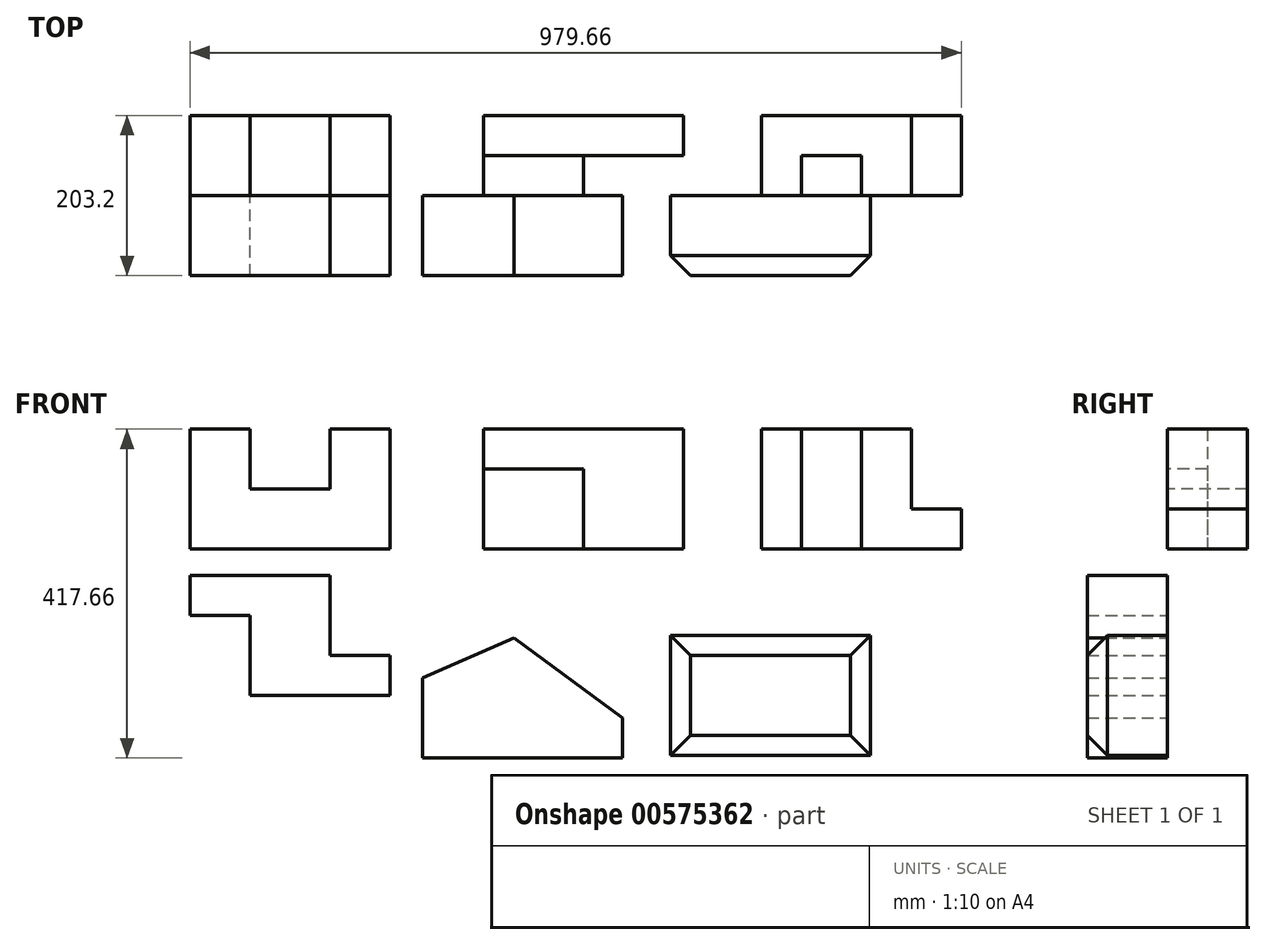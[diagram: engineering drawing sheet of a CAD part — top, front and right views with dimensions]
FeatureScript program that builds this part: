
annotation { "Feature Type Name" : "Feature", "Feature Type Description" : "" }
export const myFeature = defineFeature(function(context is Context, id is Id, definition is map)
    precondition{}
    {
        {
            var Q0;
            Q0=qCreatedBy(makeId("Front.planeOp"),FACE);
            var sketch = newSketch(context, id + "F0", { "sketchPlane" : qUnion([Q0])});
            skLineSegment(sketch, "E0", {"start": v(0, 0) * mm, "end": v(254, 0) * mm});
            skLineSegment(sketch, "E1", {"start": v(254, 0) * mm, "end": v(254, 152.4) * mm});
            skLineSegment(sketch, "E2", {"start": v(254, 152.4) * mm, "end": v(177.8, 152.4) * mm});
            skLineSegment(sketch, "E3", {"start": v(177.8, 152.4) * mm, "end": v(177.8, 76.2) * mm});
            skLineSegment(sketch, "E4", {"start": v(177.8, 76.2) * mm, "end": v(76.2, 76.2) * mm});
            skLineSegment(sketch, "E5", {"start": v(76.2, 76.2) * mm, "end": v(76.2, 152.4) * mm});
            skLineSegment(sketch, "E6", {"start": v(76.2, 152.4) * mm, "end": v(0, 152.4) * mm});
            skLineSegment(sketch, "E7", {"start": v(0, 152.4) * mm, "end": v(0, 0) * mm});
            skSolve(sketch);
        }
        {
            var Q0;
            Q0=makeQuery(id+"F0.imprint","IMPRINT",FACE,{"disambiguationData":[TD([[makeQuery(id+"F0.imprint","IMPRINT",EDGE,{"derivedFrom":sQuery(id+"F0.wireOp",EDGE,"E0")}),1.0]])]});
            extrude(context, id + "F1", {"entities" : qUnion([Q0]), "oppositeDirection" : true, "depth" : 101.6 * mm, "offsetDistance" : 25.4 * mm});
        }
        {
            var Q0;
            Q0=qCreatedBy(makeId("Top.planeOp"),FACE);
            var sketch = newSketch(context, id + "F2", { "sketchPlane" : qUnion([Q0])});
            skLineSegment(sketch, "E8", {"start": v(372.49, 0) * mm, "end": v(372.49, 101.6) * mm});
            skLineSegment(sketch, "E9", {"start": v(372.49, 101.6) * mm, "end": v(626.49, 101.6) * mm});
            skLineSegment(sketch, "E10", {"start": v(626.49, 101.6) * mm, "end": v(626.49, 50.8) * mm});
            skLineSegment(sketch, "E11", {"start": v(626.49, 50.8) * mm, "end": v(499.49, 50.8) * mm});
            skLineSegment(sketch, "E12", {"start": v(499.49, 50.8) * mm, "end": v(499.49, 0) * mm});
            skLineSegment(sketch, "E13", {"start": v(499.49, 0) * mm, "end": v(372.49, 0) * mm});
            skSolve(sketch);
        }
        {
            var Q0;
            Q0 = qSketchRegion(id + "F2", true);
            extrude(context, id + "F3", {"entities" : qUnion([Q0]), "depth" : 152.4 * mm, "offsetDistance" : 25.4 * mm});
        }
        {
            var Q0;
            Q0=makeQuery(id+"F3.opExtrude","SWEPT_FACE",FACE,{"disambiguationData":[OSD([sQuery(id+"F2.wireOp",EDGE,"E13")])]});
            var sketch = newSketch(context, id + "F4", { "sketchPlane" : qUnion([Q0])});
            skLineSegment(sketch, "E14.bottom", {"start": v(372.49, 152.4) * mm, "end": v(499.49, 152.4) * mm});
            skLineSegment(sketch, "E14.top", {"start": v(372.49, 101.6) * mm, "end": v(499.49, 101.6) * mm});
            skLineSegment(sketch, "E14.left", {"start": v(372.49, 152.4) * mm, "end": v(372.49, 101.6) * mm});
            skLineSegment(sketch, "E14.right", {"start": v(499.49, 152.4) * mm, "end": v(499.49, 101.6) * mm});
            skSolve(sketch);
        }
        {
            var Q0;
            Q0=makeQuery(id+"F4.imprint","IMPRINT",FACE,{"disambiguationData":[TD([[makeQuery(id+"F4.imprint","IMPRINT",EDGE,{"derivedFrom":sQuery(id+"F4.wireOp",EDGE,"E14.bottom")}),1.0]])]});
            extrude(context, id + "F5", {"entities" : qUnion([Q0]), "operationType" : NewBodyOperationType.REMOVE, "oppositeDirection" : true, "depth" : 50.8 * mm, "offsetDistance" : 25.4 * mm});
        }
        {
            var Q0;
            Q0=qCreatedBy(makeId("Top.planeOp"),FACE);
            var sketch = newSketch(context, id + "F6", { "sketchPlane" : qUnion([Q0])});
            skLineSegment(sketch, "E15", {"start": v(725.66, 101.6) * mm, "end": v(725.66, 0) * mm});
            skLineSegment(sketch, "E16", {"start": v(725.66, 0) * mm, "end": v(776.46, 0) * mm});
            skLineSegment(sketch, "E17", {"start": v(776.46, 0) * mm, "end": v(776.46, 50.8) * mm});
            skLineSegment(sketch, "E18", {"start": v(776.46, 50.8) * mm, "end": v(852.66, 50.8) * mm});
            skLineSegment(sketch, "E19", {"start": v(852.66, 50.8) * mm, "end": v(852.66, 0) * mm});
            skLineSegment(sketch, "E20", {"start": v(852.66, 0) * mm, "end": v(979.66, 0) * mm});
            skLineSegment(sketch, "E21", {"start": v(979.66, 0) * mm, "end": v(979.66, 101.6) * mm});
            skLineSegment(sketch, "E22", {"start": v(979.66, 101.6) * mm, "end": v(725.66, 101.6) * mm});
            skSolve(sketch);
        }
        {
            var Q0;
            Q0=makeQuery(id+"F6.imprint","IMPRINT",FACE,{"disambiguationData":[TD([[makeQuery(id+"F6.imprint","IMPRINT",EDGE,{"derivedFrom":sQuery(id+"F6.wireOp",EDGE,"E15")}),1.0]])]});
            extrude(context, id + "F7", {"entities" : qUnion([Q0]), "depth" : 152.4 * mm, "offsetDistance" : 25.4 * mm});
        }
        {
            var Q0;
            Q0=makeQuery(id+"F7.opExtrude","SWEPT_FACE",FACE,{"disambiguationData":[OSD([sQuery(id+"F6.wireOp",EDGE,"E20")])]});
            var sketch = newSketch(context, id + "F8", { "sketchPlane" : qUnion([Q0])});
            skLineSegment(sketch, "E23.bottom", {"start": v(979.66, 152.4) * mm, "end": v(916.16, 152.4) * mm});
            skLineSegment(sketch, "E23.top", {"start": v(979.66, 50.8) * mm, "end": v(916.16, 50.8) * mm});
            skLineSegment(sketch, "E23.left", {"start": v(979.66, 152.4) * mm, "end": v(979.66, 50.8) * mm});
            skLineSegment(sketch, "E23.right", {"start": v(916.16, 152.4) * mm, "end": v(916.16, 50.8) * mm});
            skSolve(sketch);
        }
        {
            var Q0;
            Q0=makeQuery(id+"F8.imprint","IMPRINT",FACE,{"disambiguationData":[TD([[makeQuery(id+"F8.imprint","IMPRINT",EDGE,{"derivedFrom":sQuery(id+"F8.wireOp",EDGE,"E23.bottom")}),-1.0]])]});
            extrude(context, id + "F9", {"entities" : qUnion([Q0]), "operationType" : NewBodyOperationType.REMOVE, "oppositeDirection" : true, "depth" : 101.6 * mm, "offsetDistance" : 25.4 * mm});
        }
        {
            var Q0;
            Q0=qCreatedBy(makeId("Front.planeOp"),FACE);
            var sketch = newSketch(context, id + "F10", { "sketchPlane" : qUnion([Q0])});
            skLineSegment(sketch, "E24", {"start": v(0, -33.79) * mm, "end": v(0, -84.59) * mm});
            skLineSegment(sketch, "E25", {"start": v(0, -84.59) * mm, "end": v(76.2, -84.59) * mm});
            skLineSegment(sketch, "E26", {"start": v(76.2, -84.59) * mm, "end": v(76.2, -186.19) * mm});
            skLineSegment(sketch, "E27", {"start": v(76.2, -186.19) * mm, "end": v(254, -186.19) * mm});
            skLineSegment(sketch, "E28", {"start": v(254, -186.19) * mm, "end": v(254, -135.39) * mm});
            skLineSegment(sketch, "E29", {"start": v(254, -135.39) * mm, "end": v(177.8, -135.39) * mm});
            skLineSegment(sketch, "E30", {"start": v(177.8, -135.39) * mm, "end": v(177.8, -33.79) * mm});
            skLineSegment(sketch, "E31", {"start": v(177.8, -33.79) * mm, "end": v(0, -33.79) * mm});
            skSolve(sketch);
        }
        {
            var Q0;
            Q0=qCreatedBy(makeId("Front.planeOp"),FACE);
            var sketch = newSketch(context, id + "F11", { "sketchPlane" : qUnion([Q0])});
            skLineSegment(sketch, "E32", {"start": v(295.1, -163.66) * mm, "end": v(295.1, -265.26) * mm});
            skLineSegment(sketch, "E33", {"start": v(295.1, -265.26) * mm, "end": v(549.1, -265.26) * mm});
            skLineSegment(sketch, "E34", {"start": v(549.1, -265.26) * mm, "end": v(549.1, -214.46) * mm});
            skLineSegment(sketch, "E35", {"start": v(549.1, -214.46) * mm, "end": v(411.49, -112.86) * mm});
            skLineSegment(sketch, "E36", {"start": v(295.1, -163.66) * mm, "end": v(411.49, -112.86) * mm});
            skSolve(sketch);
        }
        {
            var Q0;
            Q0=makeQuery(id+"F10.imprint","IMPRINT",FACE,{"disambiguationData":[TD([[makeQuery(id+"F10.imprint","IMPRINT",EDGE,{"derivedFrom":sQuery(id+"F10.wireOp",EDGE,"E24")}),1.0]])]});
            extrude(context, id + "F12", {"entities" : qUnion([Q0]), "depth" : 101.6 * mm, "offsetDistance" : 25.4 * mm});
        }
        {
            var Q0;
            Q0=makeQuery(id+"F11.imprint","IMPRINT",FACE,{"disambiguationData":[TD([[makeQuery(id+"F11.imprint","IMPRINT",EDGE,{"derivedFrom":sQuery(id+"F11.wireOp",EDGE,"E32")}),1.0]])]});
            extrude(context, id + "F13", {"entities" : qUnion([Q0]), "depth" : 101.6 * mm, "offsetDistance" : 25.4 * mm});
        }
        {
            var Q0;
            Q0=qCreatedBy(makeId("Front.planeOp"),FACE);
            var sketch = newSketch(context, id + "F14", { "sketchPlane" : qUnion([Q0])});
            skLineSegment(sketch, "E37", {"start": v(610, -109.84) * mm, "end": v(610, -262.24) * mm});
            skLineSegment(sketch, "E38", {"start": v(610, -262.24) * mm, "end": v(864, -262.24) * mm});
            skLineSegment(sketch, "E39", {"start": v(864, -262.24) * mm, "end": v(864, -109.84) * mm});
            skLineSegment(sketch, "E40", {"start": v(864, -109.84) * mm, "end": v(610, -109.84) * mm});
            skSolve(sketch);
        }
        {
            var Q0;
            Q0 = qSketchRegion(id + "F14", true);
            extrude(context, id + "F15", {"entities" : qUnion([Q0]), "depth" : 101.6 * mm, "offsetDistance" : 25.4 * mm});
        }
        {
            var Q0;
            Q0=makeQuery(id+"F15.opExtrude","CAP_FACE",FACE,{"disambiguationData":[OSD([sQuery(id+"F14.wireOp",EDGE,"E37"),sQuery(id+"F14.wireOp",EDGE,"E38"),sQuery(id+"F14.wireOp",EDGE,"E39"),sQuery(id+"F14.wireOp",EDGE,"E40")])],"isStart":false});
            chamfer(context, id + "F16", {"entities" : qUnion([Q0]), "width" : 25.4 * mm, "tangentPropagation" : true});
        }
    });
